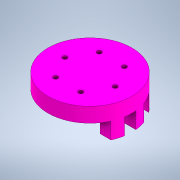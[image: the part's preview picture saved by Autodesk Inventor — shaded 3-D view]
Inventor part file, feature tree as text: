
AUTODESK INVENTOR PART (.ipt)
format: ipt  version: 2020 (Build 240168000, 168)  size: 339,456 bytes
history: native  units: mm
features: sketch x8, extrude x8, draft x2, plane x2, chamfer x1, hole x1, projected_geometry x1
ambient origin geometry x8: Origin, YZ Plane, XZ Plane, XY Plane, X Axis, Y Axis, Z Axis, Center Point
bodies: Solid1 (feature_tree)
feature tree (23):
  sketch  "Sketch1"  dims[d0=15.0mm d1=10.0mm]
  extrude  "Extrusion1"  Depth=10.0mm
  extrude  "Extrusion2"  Depth=24.0mm TaperAngle=0.0deg
  sketch  "Sketch3"  dims[d5=30.0mm d6=0.0mm d7=7.0mm d8=0.0mm]
  extrude  "Extrusion3"  Depth=7.0mm TaperAngle=0.0deg
  extrude  "Extrusion4"  Depth=7.0mm
  draft  "FaceDraft1"
  draft  "FaceDraft2"
  extrude  "Extrusion5"  Depth=2.0mm TaperAngle=0.0deg
  chamfer  "Chamfer1"  Distance=50.0mm
  plane  "Work Plane1"
  extrude  "Extrusion6"  Depth=7.0mm
  plane  "Work Plane2"
  extrude  "Extrusion7"  Depth=2.0mm TaperAngle=0.0deg
  hole  "Hole1"  [1 undecoded]
  extrude  "Extrusion8"  Depth=2.0mm
  sketch  "Sketch2"  dims[d2=40.0mm d3=24.0mm d4=0.0mm]
  projected_geometry  "Projected Loop1"
  sketch  "Sketch4"  dims[d9=11.0mm d10=7.0mm]
  sketch  "Sketch5"  dims[d13=2.0mm d14=0.0mm d15=2.0mm d16=0.0mm]
  sketch  "Sketch6"  dims[d17=3.490659mm]
  sketch  "Sketch7"  dims[d18=3.490659mm]
  sketch  "Sketch8"  dims[d19=1.0mm d20=50.0mm d21=7.0mm d22=2.0mm d23=0.0mm d24=6.4mm d25=2.0mm d26=45.0deg d27=0.2mm d28=0.2mm d29=0.2mm d30=0.2mm d31=0.2mm d32=0.2mm d33=0.2mm d34=4.9mm d35=4.9mm d36=4.9mm d37=4.9mm d38=4.9mm d39=0.0mm d40=0.0mm d41=0.2mm d42=0.2mm d43=0.2mm d44=0.2mm d45=0.2mm d46=0.2mm d47=5.5mm d48=5.5mm d49=5.5mm d50=10.0mm d51=0.0mm d52=60.0mm d54=360.0deg d56=12.0mm d57=2.2mm d58=6.0mm d59=4.0mm d60=2.0mm d61=90.0deg d62=8.0mm d63=20.594885mm d64=4.0mm d65=60.0mm d67=360.0deg d69=2.0mm d70=0.0mm d53=0.872665mm d55=0.872665mm]
note: 1 required parameter value undecoded (feature->parameter linkage not recoverable at this tier; creation-order binding heuristic only, values carry confidence <= 0.55)
